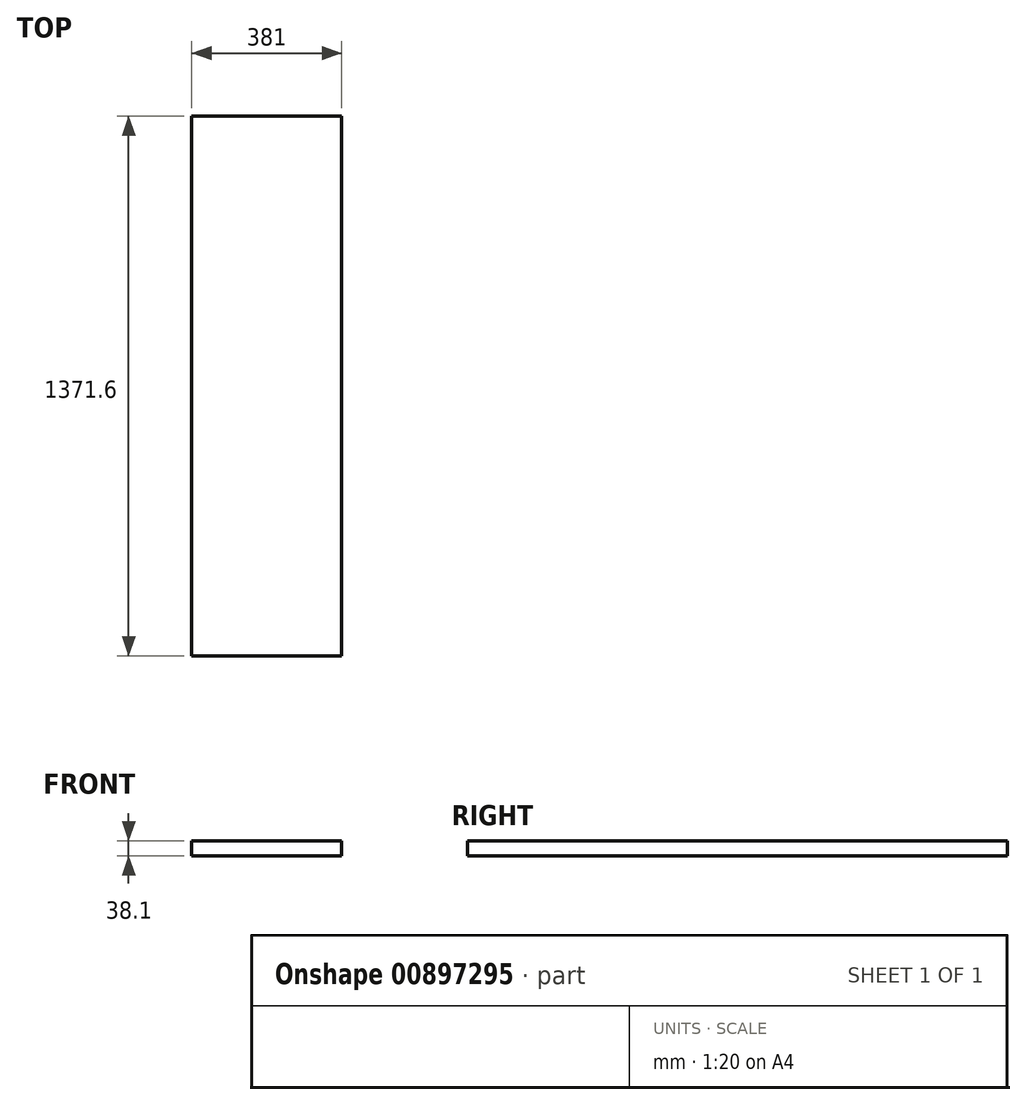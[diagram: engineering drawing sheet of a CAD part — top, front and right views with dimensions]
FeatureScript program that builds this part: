
annotation { "Feature Type Name" : "Feature", "Feature Type Description" : "" }
export const myFeature = defineFeature(function(context is Context, id is Id, definition is map)
    precondition{}
    {
        {
            var Q0;
            Q0=qCreatedBy(makeId("Top.planeOp"),FACE);
            var sketch = newSketch(context, id + "F0", { "sketchPlane" : qUnion([Q0])});
            skLineSegment(sketch, "E0.bottom", {"start": v(-387.76, 1310.46) * mm, "end": v(-6.76, 1310.46) * mm});
            skLineSegment(sketch, "E0.top", {"start": v(-387.76, -61.14) * mm, "end": v(-6.76, -61.14) * mm});
            skLineSegment(sketch, "E0.left", {"start": v(-387.76, 1310.46) * mm, "end": v(-387.76, -61.14) * mm});
            skLineSegment(sketch, "E0.right", {"start": v(-6.76, 1310.46) * mm, "end": v(-6.76, -61.14) * mm});
            skSolve(sketch);
        }
        {
            var Q0;
            Q0=makeQuery(id+"F0.imprint","IMPRINT",FACE,{"disambiguationData":[TD([[makeQuery(id+"F0.imprint","IMPRINT",EDGE,{"derivedFrom":sQuery(id+"F0.wireOp",EDGE,"E0.bottom")}),-1.0]])]});
            extrude(context, id + "F1", {"entities" : qUnion([Q0]), "depth" : 38.1 * mm, "offsetDistance" : 25.4 * mm});
        }
    });
